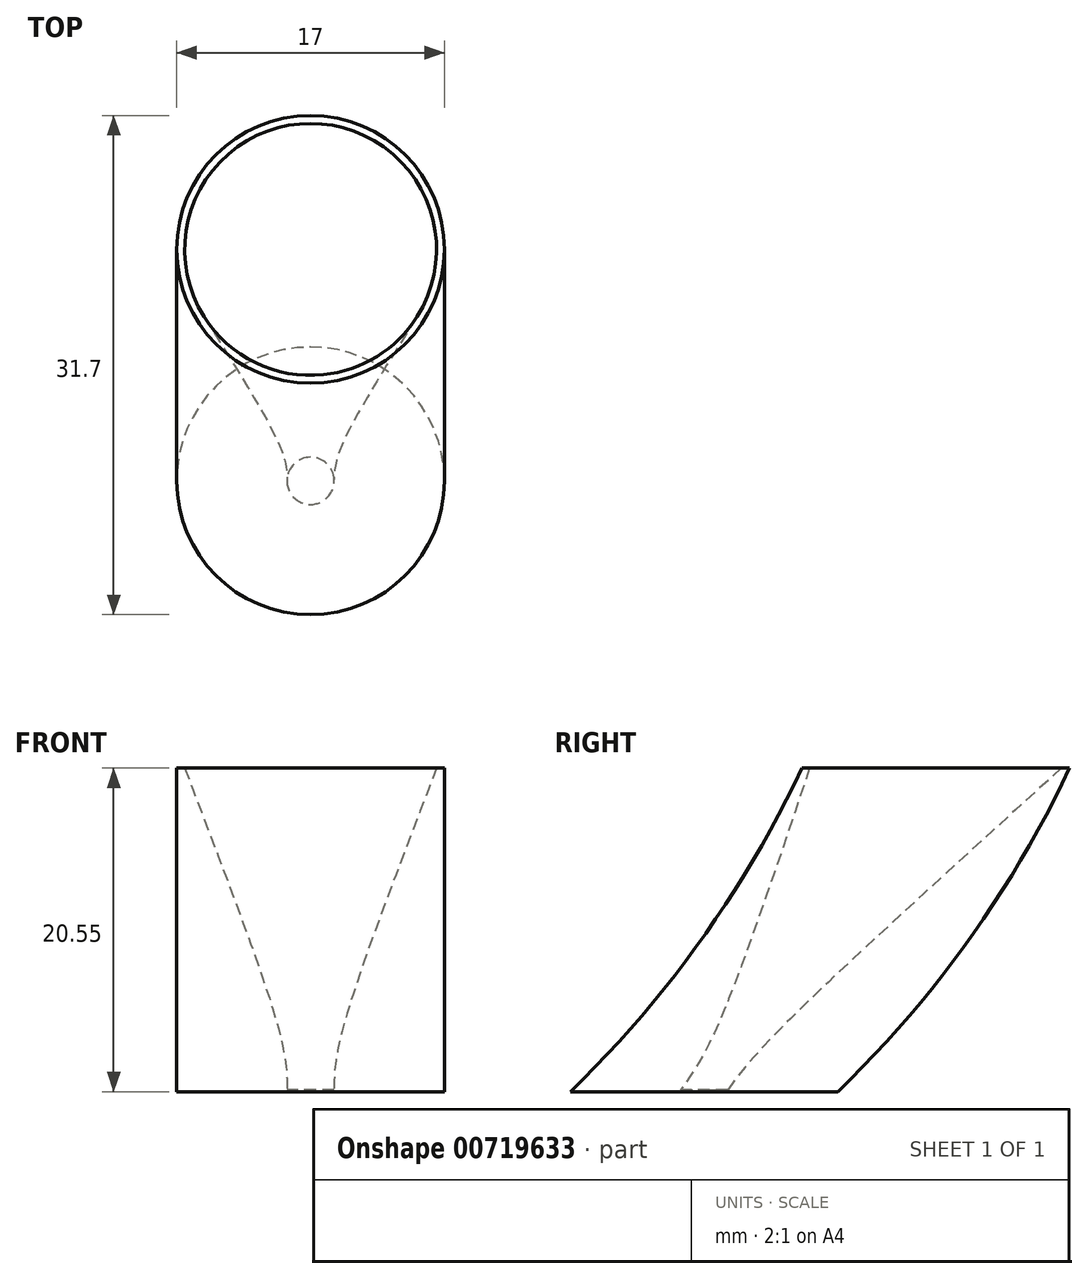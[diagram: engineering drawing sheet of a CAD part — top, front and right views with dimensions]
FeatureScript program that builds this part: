
annotation { "Feature Type Name" : "Feature", "Feature Type Description" : "" }
export const myFeature = defineFeature(function(context is Context, id is Id, definition is map)
    precondition{}
    {
        {
            var Q0;
            Q0=qCreatedBy(makeId("Top.planeOp"),FACE);
            var sketch = newSketch(context, id + "F0", { "sketchPlane" : qUnion([Q0])});
            skCircle(sketch, "E0", {"center": v(0, 0) * mm, "radius": 8.5 * mm});
            skSolve(sketch);
        }
        {
            var Q0;
            Q0=qCreatedBy(makeId("Right.planeOp"),FACE);
            var sketch = newSketch(context, id + "F1", { "sketchPlane" : qUnion([Q0])});
            skArc(sketch, "E1", {"start": v(0, 0) * mm, "mid": v(8.29, 9.6) * mm, "end": v(14.7, 20.55) * mm});
            skSolve(sketch);
        }
        {
            var Q0;
            Q0=qSketchRegion(id+"F0",true);
            var Q1;
            Q1=qConstructionFilter(qBodyType(qCreatedBy(id+"F1",EDGE),BodyType.WIRE),ConstructionObject.NO);
            sweep(context, id + "F2", {"profiles" : qUnion([Q0]), "path" : qUnion([Q1]), "keepProfileOrientation" : true});
        }
        {
            var Q0;
            Q0=makeQuery(id+"F2.opSweep","CAP_FACE",FACE,{"disambiguationData":[OSD([sQuery(id+"F0.wireOp",EDGE,"E0"),sQuery(id+"F1.wireOp",VERTEX,"E1.end")])],"isStart":false});
            var sketch = newSketch(context, id + "F3", { "sketchPlane" : qUnion([Q0])});
            skCircle(sketch, "E2", {"center": v(0, 14.7) * mm, "radius": 8 * mm});
            skSolve(sketch);
        }
        {
            var Q0;
            Q0=qCreatedBy(makeId("Top.planeOp"),FACE);
            cPlane(context, id + "F4", {"entities" : qUnion([Q0]), "cplaneType" : CPlaneType.OFFSET, "offset" : 0.1 * mm, "width" : 150 * mm, "height" : 150 * mm});
        }
        {
            var Q0;
            Q0=qCreatedBy(id+"F4.planeOp",FACE);
            var sketch = newSketch(context, id + "F5", { "sketchPlane" : qUnion([Q0])});
            skCircle(sketch, "E3", {"center": v(0, 0) * mm, "radius": 1.5 * mm});
            skSolve(sketch);
        }
        {
            var Q0;
            Q0=makeQuery(id+"F2.opSweep","CAP_FACE",FACE,{"disambiguationData":[OSD([sQuery(id+"F0.wireOp",EDGE,"E0"),sQuery(id+"F1.wireOp",VERTEX,"E1.end")])],"isStart":false});
            var sketch = newSketch(context, id + "F6", { "sketchPlane" : qUnion([Q0])});
            skCircle(sketch, "E4", {"center": v(0, 14.7) * mm, "radius": 8 * mm});
            skSolve(sketch);
        }
        {
            var Q1;
            Q1 = qSketchRegion(id + "F5", true);
            var Q2;
            Q2 = qSketchRegion(id + "F6", true);
            loft(context, id + "F7", {"operationType" : NewBodyOperationType.REMOVE, "sheetProfilesArray" : [{ "sheetProfileEntities" : qUnion([Q1]) }, { "sheetProfileEntities" : qUnion([Q2]) }]});
        }
    });
